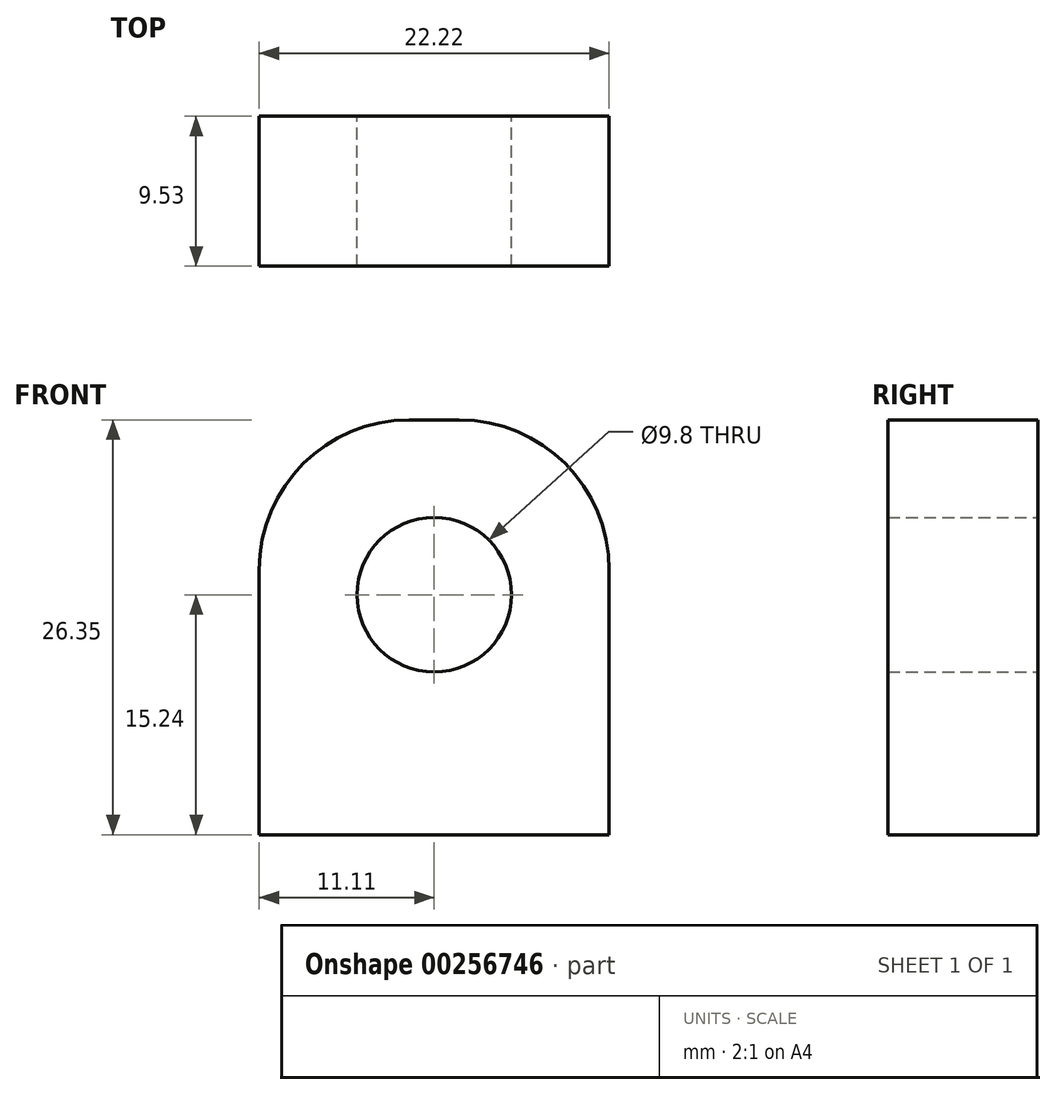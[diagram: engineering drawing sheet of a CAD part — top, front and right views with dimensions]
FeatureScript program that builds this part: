
annotation { "Feature Type Name" : "Feature", "Feature Type Description" : "" }
export const myFeature = defineFeature(function(context is Context, id is Id, definition is map)
    precondition{}
    {
        {
            var Q0;
            Q0=qCreatedBy(makeId("Front.planeOp"),FACE);
            var sketch = newSketch(context, id + "F0", { "sketchPlane" : qUnion([Q0])});
            skLineSegment(sketch, "E0.bottom", {"start": v(-11.11, 0) * mm, "end": v(11.11, 0) * mm});
            skLineSegment(sketch, "E0.top", {"start": v(-11.11, 26.35) * mm, "end": v(11.11, 26.35) * mm});
            skLineSegment(sketch, "E0.left", {"start": v(-11.11, 0) * mm, "end": v(-11.11, 26.35) * mm});
            skLineSegment(sketch, "E0.right", {"start": v(11.11, 0) * mm, "end": v(11.11, 26.35) * mm});
            skCircle(sketch, "E1", {"center": v(0, 15.24) * mm, "radius": 4.9 * mm});
            skSolve(sketch);
        }
        {
            var Q0;
            Q0=makeQuery(id+"F0.imprint","IMPRINT",FACE,{"disambiguationData":[TD([[makeQuery(id+"F0.imprint","IMPRINT",EDGE,{"derivedFrom":sQuery(id+"F0.wireOp",EDGE,"E0.bottom")}),1.0]])]});
            extrude(context, id + "F1", {"entities" : qUnion([Q0]), "depth" : 9.52 * mm});
        }
        {
            var Q0;
            Q0=makeQuery(id+"F1.opExtrude","SWEPT_EDGE",EDGE,{"disambiguationData":[OSD([sQuery(id+"F0.wireOp",EDGE,"E0.top"),sQuery(id+"F0.wireOp",EDGE,"E0.right")])]});
            var Q1;
            Q1=makeQuery(id+"F1.opExtrude","SWEPT_EDGE",EDGE,{"disambiguationData":[OSD([sQuery(id+"F0.wireOp",EDGE,"E0.top"),sQuery(id+"F0.wireOp",EDGE,"E0.left")])]});
            fillet(context, id + "F2", {"entities" : qUnion([Q0, Q1]), "radius" : 9.52 * mm, "tangentPropagation" : true, "allowEdgeOverflow" : false});
        }
    });
